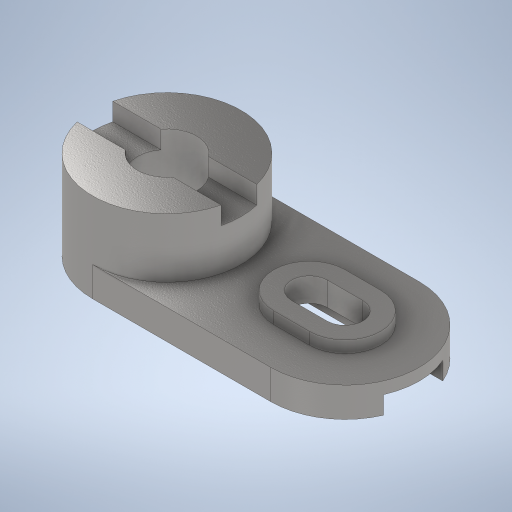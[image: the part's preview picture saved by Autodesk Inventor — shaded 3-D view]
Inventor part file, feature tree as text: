
AUTODESK INVENTOR PART (.ipt)
format: ipt  version: 2024 (Build 280153000, 153)  size: 360,960 bytes
history: native  units: mm
features: extrude x7, sketch x5, plane x1, projected_geometry x1
ambient origin geometry x8: Origin, YZ Plane, XZ Plane, XY Plane, X Axis, Y Axis, Z Axis, Center Point
bodies: Volumenkörper1 (feature_tree)
feature tree (14):
  sketch  "Skizze1"  dims[d1=25.0mm d2=50.0mm]
  extrude  "Extrusion1"  Depth=50.0mm
  extrude  "Extrusion2"  Depth=10.0mm TaperAngle=0.0deg
  extrude  "Extrusion4"  Depth=12.0mm
  extrude  "Extrusion5"  Depth=20.0mm
  sketch  "Skizze5"  dims[d12=6.0mm d13=0.0mm d14=20.0mm]
  extrude  "Extrusion6"  Depth=12.0mm
  extrude  "Extrusion7"  Depth=60.0mm
  plane  "Arbeitsebene2"
  extrude  "Extrusion8"  Depth=6.0mm
  sketch  "Skizze3"  dims[d3=60.0mm d4=10.0mm d5=0.0mm]
  projected_geometry  "Projizierte Kontur1"
  sketch  "Skizze4"  dims[d6=30.0mm d7=0.0mm d11=12.0mm]
  sketch  "Skizze6"  dims[d15=6.0mm d16=0.0mm d17=12.0mm d18=60.0mm d19=6.0mm d20=12.0mm d21=10.0mm d22=0.0mm d23=4.0mm d24=0.0mm d25=85.0mm d26=20.0mm d27=4.0mm d28=4.0mm d29=0.0mm]
